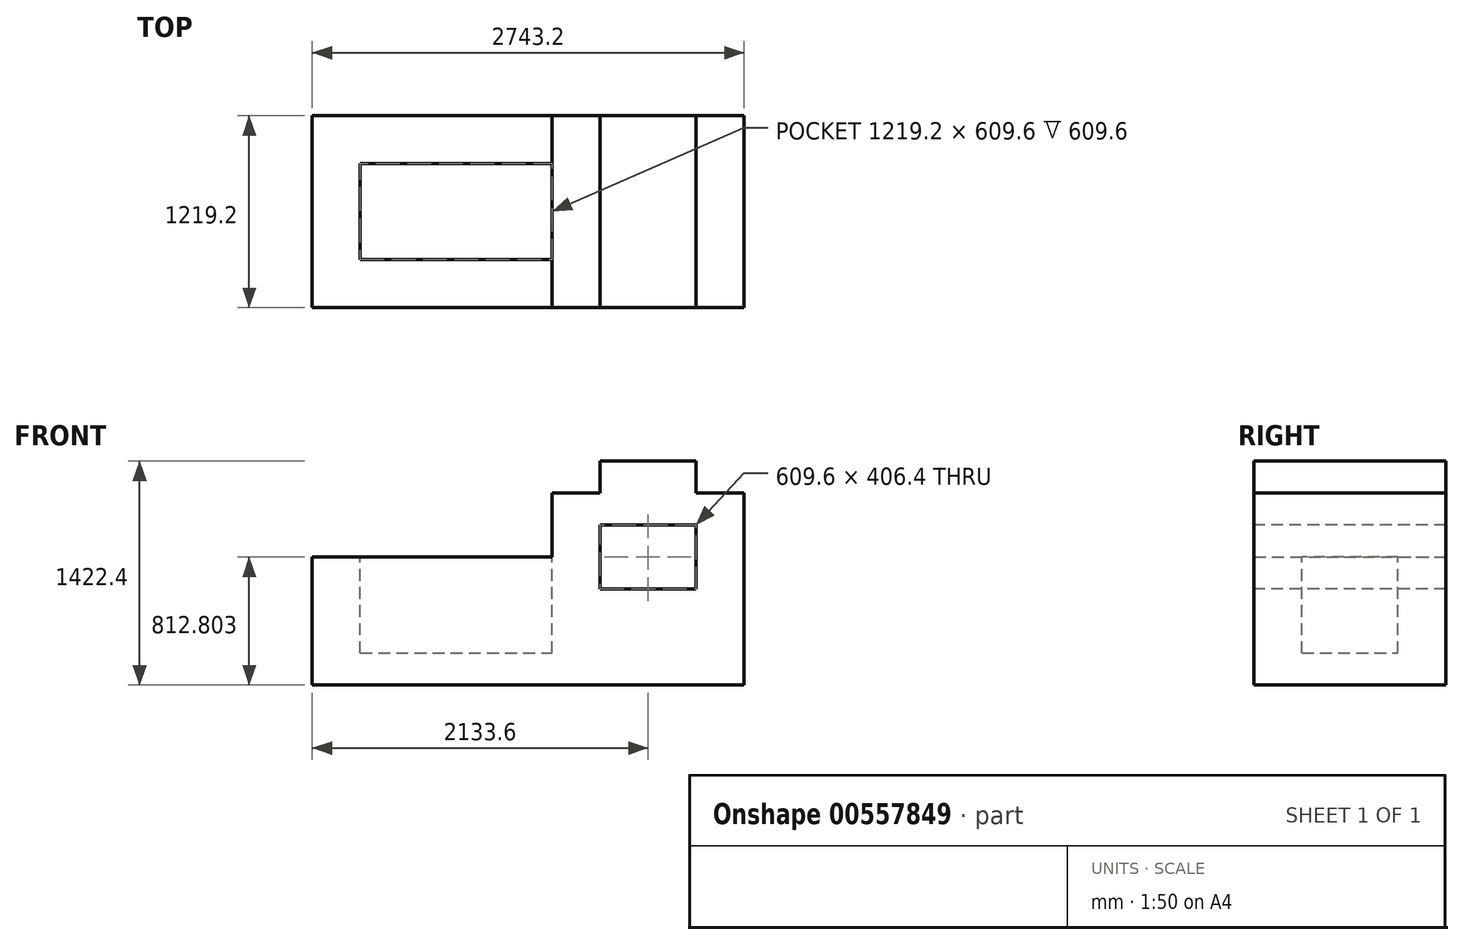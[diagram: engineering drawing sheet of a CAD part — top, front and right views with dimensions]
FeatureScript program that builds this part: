
annotation { "Feature Type Name" : "Feature", "Feature Type Description" : "" }
export const myFeature = defineFeature(function(context is Context, id is Id, definition is map)
    precondition{}
    {
        {
            var Q0;
            Q0=qCreatedBy(makeId("Front.planeOp"),FACE);
            var sketch = newSketch(context, id + "F0", { "sketchPlane" : qUnion([Q0])});
            skLineSegment(sketch, "E0", {"start": v(-118.57, 12.77) * mm, "end": v(2624.63, 12.77) * mm});
            skLineSegment(sketch, "E1", {"start": v(2624.63, 12.77) * mm, "end": v(2624.63, 1231.97) * mm});
            skLineSegment(sketch, "E2", {"start": v(2624.63, 1231.97) * mm, "end": v(2319.83, 1231.97) * mm});
            skPoint(sketch, "E3.end.orphan", {"position": v(1710.23, 1231.97) * mm});
            skLineSegment(sketch, "E4", {"start": v(2319.83, 1231.97) * mm, "end": v(2319.83, 1435.17) * mm});
            skLineSegment(sketch, "E5", {"start": v(2319.83, 1435.17) * mm, "end": v(1710.23, 1435.17) * mm});
            skLineSegment(sketch, "E6", {"start": v(1710.23, 1435.17) * mm, "end": v(1710.23, 1231.97) * mm});
            skLineSegment(sketch, "E7", {"start": v(1710.23, 1231.97) * mm, "end": v(1405.43, 1231.97) * mm});
            skLineSegment(sketch, "E8", {"start": v(1405.43, 1231.97) * mm, "end": v(1405.43, 825.57) * mm});
            skLineSegment(sketch, "E9", {"start": v(1405.43, 825.57) * mm, "end": v(-118.57, 825.57) * mm});
            skLineSegment(sketch, "E10", {"start": v(-118.57, 825.57) * mm, "end": v(-118.57, 12.77) * mm});
            skSolve(sketch);
        }
        {
            var Q0;
            Q0=makeQuery(id+"F0.imprint","IMPRINT",FACE,{"disambiguationData":[TD([[makeQuery(id+"F0.imprint","IMPRINT",EDGE,{"derivedFrom":sQuery(id+"F0.wireOp",EDGE,"E0")}),1.0]])]});
            extrude(context, id + "F1", {"entities" : qUnion([Q0]), "depth" : 1219.2 * mm, "offsetDistance" : 25.4 * mm});
        }
        {
            var Q0;
            Q0=makeQuery(id+"F1.opExtrude","CAP_FACE",FACE,{"disambiguationData":[OSD([sQuery(id+"F0.wireOp",EDGE,"E0"),sQuery(id+"F0.wireOp",EDGE,"E1"),sQuery(id+"F0.wireOp",EDGE,"E2"),sQuery(id+"F0.wireOp",EDGE,"E4"),sQuery(id+"F0.wireOp",EDGE,"E5"),sQuery(id+"F0.wireOp",EDGE,"E6"),sQuery(id+"F0.wireOp",EDGE,"E7"),sQuery(id+"F0.wireOp",EDGE,"E8"),sQuery(id+"F0.wireOp",EDGE,"E9"),sQuery(id+"F0.wireOp",EDGE,"E10")])],"isStart":false});
            var sketch = newSketch(context, id + "F2", { "sketchPlane" : qUnion([Q0])});
            skLineSegment(sketch, "E11.bottom", {"start": v(1710.23, 1028.77) * mm, "end": v(2319.83, 1028.77) * mm});
            skLineSegment(sketch, "E11.top", {"start": v(1710.23, 622.37) * mm, "end": v(2319.83, 622.37) * mm});
            skLineSegment(sketch, "E11.left", {"start": v(1710.23, 1028.77) * mm, "end": v(1710.23, 622.37) * mm});
            skLineSegment(sketch, "E11.right", {"start": v(2319.83, 1028.77) * mm, "end": v(2319.83, 622.37) * mm});
            skSolve(sketch);
        }
        {
            var Q0;
            Q0=makeQuery(id+"F2.imprint","IMPRINT",FACE,{"disambiguationData":[TD([[makeQuery(id+"F2.imprint","IMPRINT",EDGE,{"derivedFrom":sQuery(id+"F2.wireOp",EDGE,"E11.bottom")}),-1.0]])]});
            extrude(context, id + "F3", {"entities" : qUnion([Q0]), "operationType" : NewBodyOperationType.REMOVE, "endBound" : BoundingType.THROUGH_ALL, "oppositeDirection" : true, "depth" : 25.4 * mm, "offsetDistance" : 25.4 * mm});
        }
        {
            var Q0;
            Q0=makeQuery(id+"F1.opExtrude","SWEPT_FACE",FACE,{"disambiguationData":[OSD([sQuery(id+"F0.wireOp",EDGE,"E9")])]});
            var sketch = newSketch(context, id + "F4", { "sketchPlane" : qUnion([Q0])});
            skLineSegment(sketch, "E12.bottom", {"start": v(186.23, -304.8) * mm, "end": v(1405.43, -304.8) * mm});
            skLineSegment(sketch, "E12.top", {"start": v(186.23, -914.4) * mm, "end": v(1405.43, -914.4) * mm});
            skLineSegment(sketch, "E12.left", {"start": v(186.23, -304.8) * mm, "end": v(186.23, -914.4) * mm});
            skLineSegment(sketch, "E12.right", {"start": v(1405.43, -304.8) * mm, "end": v(1405.43, -914.4) * mm});
            skSolve(sketch);
        }
        {
            var Q0;
            Q0=makeQuery(id+"F4.imprint","IMPRINT",FACE,{"disambiguationData":[TD([[makeQuery(id+"F4.imprint","IMPRINT",EDGE,{"derivedFrom":sQuery(id+"F4.wireOp",EDGE,"E12.bottom")}),-1.0]])]});
            extrude(context, id + "F5", {"entities" : qUnion([Q0]), "operationType" : NewBodyOperationType.REMOVE, "oppositeDirection" : true, "depth" : 609.6 * mm, "offsetDistance" : 25.4 * mm});
        }
    });
